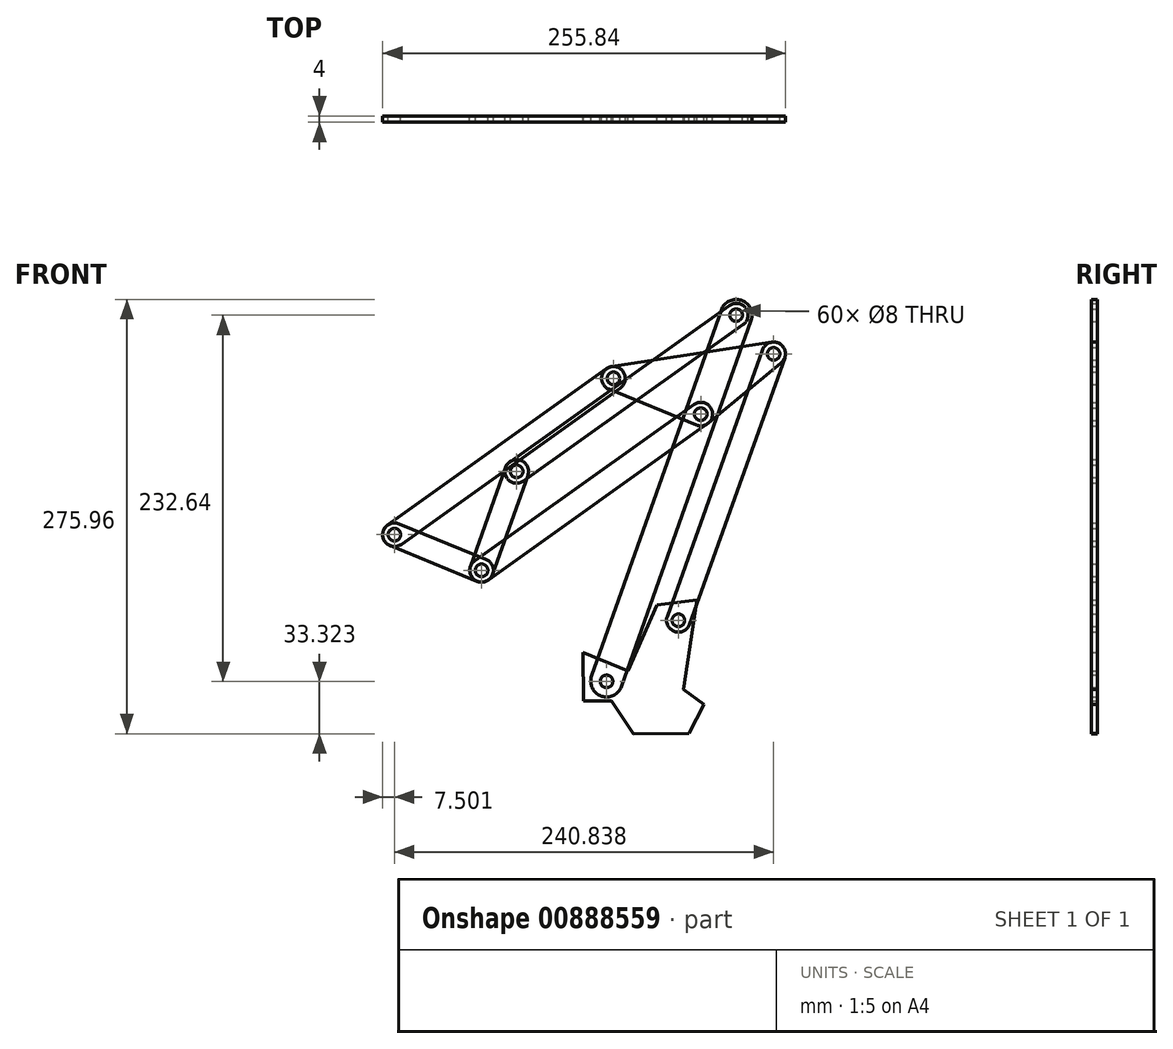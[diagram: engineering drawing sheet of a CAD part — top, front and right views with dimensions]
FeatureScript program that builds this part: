
annotation { "Feature Type Name" : "Feature", "Feature Type Description" : "" }
export const myFeature = defineFeature(function(context is Context, id is Id, definition is map)
    precondition{}
    {
        {
            var Q0;
            Q0=qCreatedBy(makeId("Front.planeOp"),FACE);
            var sketch = newSketch(context, id + "F0", { "sketchPlane" : qUnion([Q0])});
            skCircle(sketch, "E0", {"center": v(-65.08, -32.12) * mm, "radius": 6 * mm});
            skCircle(sketch, "E1", {"center": v(-120.42, -9.5) * mm, "radius": 6 * mm});
            skLineSegment(sketch, "E2", {"start": v(-120.42, -9.5) * mm, "end": v(-65.08, -32.12) * mm});
            skLineSegment(sketch, "E3", {"start": v(-65.08, -32.12) * mm, "end": v(74.1, 67.1) * mm});
            skCircle(sketch, "E4", {"center": v(74.1, 67.1) * mm, "radius": 6 * mm});
            skCircle(sketch, "E5", {"center": v(-42.78, 30.7) * mm, "radius": 6 * mm});
            skLineSegment(sketch, "E6", {"start": v(-65.08, -32.12) * mm, "end": v(-42.78, 30.7) * mm});
            skLineSegment(sketch, "E7", {"start": v(18.68, 89.85) * mm, "end": v(-120.42, -9.5) * mm});
            skCircle(sketch, "E8", {"center": v(18.68, 89.85) * mm, "radius": 6 * mm});
            skLineSegment(sketch, "E9", {"start": v(74.1, 67.1) * mm, "end": v(14.28, -102.66) * mm});
            skLineSegment(sketch, "E10", {"start": v(96.64, 129.98) * mm, "end": v(74.1, 67.1) * mm});
            skCircle(sketch, "E11", {"center": v(120.42, 105.37) * mm, "radius": 6 * mm});
            skLineSegment(sketch, "E12", {"start": v(120.42, 105.37) * mm, "end": v(18.68, 89.85) * mm});
            skLineSegment(sketch, "E13", {"start": v(74.1, 67.1) * mm, "end": v(120.42, 105.37) * mm});
            skLineSegment(sketch, "E14", {"start": v(18.68, 89.85) * mm, "end": v(74.1, 67.1) * mm});
            skLineSegment(sketch, "E15", {"start": v(96.64, 129.98) * mm, "end": v(-42.78, 30.7) * mm});
            skLineSegment(sketch, "E16", {"start": v(120.42, 105.37) * mm, "end": v(59.92, -63.84) * mm});
            skCircle(sketch, "E17", {"center": v(14.28, -102.66) * mm, "radius": 6 * mm});
            skCircle(sketch, "E18", {"center": v(59.92, -63.84) * mm, "radius": 6 * mm});
            skLineSegment(sketch, "E19", {"start": v(-0.52, -84.13) * mm, "end": v(-0.28, -115.17) * mm});
            skLineSegment(sketch, "E20", {"start": v(-0.28, -115.17) * mm, "end": v(17.4, -115.04) * mm});
            skLineSegment(sketch, "E21", {"start": v(17.4, -115.04) * mm, "end": v(31.55, -135.98) * mm});
            skLineSegment(sketch, "E22", {"start": v(31.55, -135.98) * mm, "end": v(66.6, -135.71) * mm});
            skLineSegment(sketch, "E23", {"start": v(66.6, -135.71) * mm, "end": v(76.3, -117.34) * mm});
            skLineSegment(sketch, "E24", {"start": v(76.3, -117.34) * mm, "end": v(63, -107.76) * mm});
            skLineSegment(sketch, "E25", {"start": v(63, -107.76) * mm, "end": v(71.78, -50.98) * mm});
            skLineSegment(sketch, "E26", {"start": v(71.78, -50.98) * mm, "end": v(46.28, -54.1) * mm});
            skLineSegment(sketch, "E27", {"start": v(46.28, -54.1) * mm, "end": v(28.01, -95.9) * mm});
            skLineSegment(sketch, "E28", {"start": v(28.01, -95.9) * mm, "end": v(-0.52, -84.13) * mm});
            skCircle(sketch, "E29", {"center": v(96.64, 129.98) * mm, "radius": 6 * mm});
            skSolve(sketch);
        }
        {
            var Q0;
            Q0=qCreatedBy(makeId("Front.planeOp"),FACE);
            var sketch = newSketch(context, id + "F1", { "sketchPlane" : qUnion([Q0])});
            skCircle(sketch, "E30", {"center": v(-120.42, -9.5) * mm, "radius": 4 * mm});
            skCircle(sketch, "E31", {"center": v(-65.08, -32.12) * mm, "radius": 4 * mm});
            skArc(sketch, "E32", {"start": v(-67.92, -39.07) * mm, "mid": v(-58.14, -34.96) * mm, "end": v(-62.25, -25.18) * mm});
            skArc(sketch, "E33", {"start": v(-117.58, -2.56) * mm, "mid": v(-127.36, -6.66) * mm, "end": v(-123.26, -16.44) * mm});
            skLineSegment(sketch, "E34", {"start": v(-123.26, -16.44) * mm, "end": v(-67.92, -39.07) * mm});
            skLineSegment(sketch, "E35", {"start": v(-117.58, -2.56) * mm, "end": v(-62.25, -25.18) * mm});
            skCircle(sketch, "E36.0", {"center": v(-120.42, -9.5) * mm, "radius": 6 * mm, "construction": true});
            skCircle(sketch, "E37.0", {"center": v(-65.08, -32.12) * mm, "radius": 6 * mm, "construction": true});
            skSolve(sketch);
        }
        {
            var Q0;
            Q0=makeQuery(id+"F1.imprint","IMPRINT",FACE,{"disambiguationData":[TD([[makeQuery(id+"F1.imprint","IMPRINT",EDGE,{"derivedFrom":sQuery(id+"F1.wireOp",EDGE,"E30")}),-1.0]])]});
            extrude(context, id + "F2", {"entities" : qUnion([Q0]), "depth" : 4 * mm, "offsetDistance" : 25 * mm});
        }
        {
            var Q0;
            Q0=qCreatedBy(makeId("Front.planeOp"),FACE);
            var sketch = newSketch(context, id + "F3", { "sketchPlane" : qUnion([Q0])});
            skCircle(sketch, "E38", {"center": v(-42.78, 30.7) * mm, "radius": 4 * mm});
            skArc(sketch, "E39", {"start": v(-72.15, -29.61) * mm, "mid": v(-67.6, -39.2) * mm, "end": v(-58.02, -34.63) * mm});
            skArc(sketch, "E40", {"start": v(-35.7, 28.2) * mm, "mid": v(-40.27, 37.77) * mm, "end": v(-49.84, 33.21) * mm});
            skCircle(sketch, "E41", {"center": v(-65.08, -32.12) * mm, "radius": 4 * mm});
            skLineSegment(sketch, "E42", {"start": v(-35.7, 28.2) * mm, "end": v(-58.02, -34.63) * mm});
            skLineSegment(sketch, "E43", {"start": v(-49.84, 33.21) * mm, "end": v(-72.15, -29.61) * mm});
            skCircle(sketch, "E44.0", {"center": v(-42.78, 30.7) * mm, "radius": 6 * mm, "construction": true});
            skCircle(sketch, "E45.0", {"center": v(-65.08, -32.12) * mm, "radius": 6 * mm, "construction": true});
            skSolve(sketch);
        }
        {
            var Q0;
            Q0=makeQuery(id+"F3.imprint","IMPRINT",FACE,{"disambiguationData":[TD([[makeQuery(id+"F3.imprint","IMPRINT",EDGE,{"derivedFrom":sQuery(id+"F3.wireOp",EDGE,"E38")}),-1.0]])]});
            extrude(context, id + "F4", {"entities" : qUnion([Q0]), "depth" : 4 * mm, "offsetDistance" : 25 * mm});
        }
        {
            var Q0;
            Q0=qCreatedBy(makeId("Front.planeOp"),FACE);
            var sketch = newSketch(context, id + "F5", { "sketchPlane" : qUnion([Q0])});
            skCircle(sketch, "E46", {"center": v(-120.42, -9.5) * mm, "radius": 4 * mm});
            skArc(sketch, "E47", {"start": v(-124.78, -3.4) * mm, "mid": v(-126.52, -13.86) * mm, "end": v(-116.06, -15.6) * mm});
            skArc(sketch, "E48", {"start": v(23.04, 83.75) * mm, "mid": v(24.78, 94.2) * mm, "end": v(14.32, 95.95) * mm});
            skCircle(sketch, "E49", {"center": v(18.68, 89.85) * mm, "radius": 4 * mm});
            skLineSegment(sketch, "E50", {"start": v(-124.78, -3.4) * mm, "end": v(14.32, 95.95) * mm});
            skLineSegment(sketch, "E51", {"start": v(-116.06, -15.6) * mm, "end": v(23.04, 83.75) * mm});
            skCircle(sketch, "E52.0", {"center": v(18.68, 89.85) * mm, "radius": 6 * mm, "construction": true});
            skCircle(sketch, "E53.0", {"center": v(-120.42, -9.5) * mm, "radius": 6 * mm, "construction": true});
            skSolve(sketch);
        }
        {
            var Q0;
            Q0=makeQuery(id+"F5.imprint","IMPRINT",FACE,{"disambiguationData":[TD([[makeQuery(id+"F5.imprint","IMPRINT",EDGE,{"derivedFrom":sQuery(id+"F5.wireOp",EDGE,"E46")}),-1.0]])]});
            extrude(context, id + "F6", {"entities" : qUnion([Q0]), "depth" : 4 * mm, "offsetDistance" : 25 * mm});
        }
        {
            var Q0;
            Q0=qCreatedBy(makeId("Front.planeOp"),FACE);
            var sketch = newSketch(context, id + "F7", { "sketchPlane" : qUnion([Q0])});
            skCircle(sketch, "E54", {"center": v(74.1, 67.1) * mm, "radius": 4 * mm});
            skArc(sketch, "E55", {"start": v(78.46, 60.98) * mm, "mid": v(80.22, 71.44) * mm, "end": v(69.75, 73.2) * mm});
            skCircle(sketch, "E56", {"center": v(-65.08, -32.12) * mm, "radius": 4 * mm});
            skArc(sketch, "E57", {"start": v(-69.44, -26.02) * mm, "mid": v(-71.2, -36.48) * mm, "end": v(-60.73, -38.23) * mm});
            skLineSegment(sketch, "E58", {"start": v(-69.44, -26.02) * mm, "end": v(69.75, 73.2) * mm});
            skLineSegment(sketch, "E59", {"start": v(-60.73, -38.23) * mm, "end": v(78.46, 60.98) * mm});
            skSolve(sketch);
        }
        {
            var Q0;
            Q0=makeQuery(id+"F7.imprint","IMPRINT",FACE,{"disambiguationData":[TD([[makeQuery(id+"F7.imprint","IMPRINT",EDGE,{"derivedFrom":sQuery(id+"F7.wireOp",EDGE,"E54")}),-1.0]])]});
            extrude(context, id + "F8", {"entities" : qUnion([Q0]), "depth" : 4 * mm, "offsetDistance" : 25 * mm});
        }
        {
            var Q0;
            Q0=qCreatedBy(makeId("Front.planeOp"),FACE);
            var sketch = newSketch(context, id + "F9", { "sketchPlane" : qUnion([Q0])});
            skArc(sketch, "E60", {"start": v(71.26, 60.15) * mm, "mid": v(75.23, 59.68) * mm, "end": v(78.89, 61.31) * mm});
            skArc(sketch, "E61", {"start": v(125.2, 99.6) * mm, "mid": v(127.26, 108.44) * mm, "end": v(119.29, 112.79) * mm});
            skArc(sketch, "E62", {"start": v(17.55, 97.26) * mm, "mid": v(11.23, 90.74) * mm, "end": v(15.83, 82.91) * mm});
            skLineSegment(sketch, "E63", {"start": v(15.83, 82.91) * mm, "end": v(71.26, 60.15) * mm});
            skLineSegment(sketch, "E64", {"start": v(17.55, 97.26) * mm, "end": v(119.29, 112.79) * mm});
            skLineSegment(sketch, "E65.trimOffspring", {"start": v(78.89, 61.31) * mm, "end": v(125.2, 99.6) * mm});
            skCircle(sketch, "E66", {"center": v(120.42, 105.37) * mm, "radius": 4 * mm});
            skCircle(sketch, "E67", {"center": v(74.1, 67.1) * mm, "radius": 4 * mm});
            skCircle(sketch, "E68", {"center": v(18.68, 89.85) * mm, "radius": 4 * mm});
            skSolve(sketch);
        }
        {
            var Q0;
            Q0=makeQuery(id+"F9.imprint","IMPRINT",FACE,{"disambiguationData":[TD([[makeQuery(id+"F9.imprint","IMPRINT",EDGE,{"derivedFrom":sQuery(id+"F9.wireOp",EDGE,"E60")}),1.0]])]});
            extrude(context, id + "F10", {"entities" : qUnion([Q0]), "depth" : 4 * mm, "offsetDistance" : 25 * mm});
        }
        {
            var Q0;
            Q0=qCreatedBy(makeId("Front.planeOp"),FACE);
            var sketch = newSketch(context, id + "F11", { "sketchPlane" : qUnion([Q0])});
            skCircle(sketch, "E69.0", {"center": v(96.64, 129.98) * mm, "radius": 6 * mm, "construction": true});
            skCircle(sketch, "E70.0", {"center": v(74.1, 67.1) * mm, "radius": 6 * mm, "construction": true});
            skCircle(sketch, "E71.0", {"center": v(14.28, -102.66) * mm, "radius": 6 * mm, "construction": true});
            skCircle(sketch, "E72", {"center": v(14.28, -102.66) * mm, "radius": 4 * mm});
            skCircle(sketch, "E73", {"center": v(74.1, 67.1) * mm, "radius": 4 * mm});
            skCircle(sketch, "E74", {"center": v(96.64, 129.98) * mm, "radius": 4 * mm});
            skArc(sketch, "E75", {"start": v(106.07, 126.65) * mm, "mid": v(99.98, 139.41) * mm, "end": v(87.21, 133.32) * mm});
            skArc(sketch, "E76", {"start": v(4.86, -99.32) * mm, "mid": v(10.95, -112.08) * mm, "end": v(23.7, -106) * mm});
            skLineSegment(sketch, "E77", {"start": v(106.07, 126.65) * mm, "end": v(23.7, -106) * mm});
            skLineSegment(sketch, "E78", {"start": v(87.21, 133.32) * mm, "end": v(4.86, -99.32) * mm});
            skSolve(sketch);
        }
        {
            var Q0;
            Q0 = qSketchRegion(id + "F11", true);
            extrude(context, id + "F12", {"entities" : qUnion([Q0]), "depth" : 4 * mm, "offsetDistance" : 25 * mm});
        }
        {
            var Q0;
            Q0=qCreatedBy(makeId("Front.planeOp"),FACE);
            var sketch = newSketch(context, id + "F13", { "sketchPlane" : qUnion([Q0])});
            skCircle(sketch, "E79.0", {"center": v(-42.78, 30.7) * mm, "radius": 6 * mm, "construction": true});
            skCircle(sketch, "E80.0", {"center": v(96.64, 129.98) * mm, "radius": 6 * mm, "construction": true});
            skArc(sketch, "E81", {"start": v(-47.13, 36.81) * mm, "mid": v(-48.88, 26.35) * mm, "end": v(-38.43, 24.6) * mm});
            skArc(sketch, "E82", {"start": v(101, 123.87) * mm, "mid": v(102.75, 134.33) * mm, "end": v(92.3, 136.1) * mm});
            skCircle(sketch, "E83", {"center": v(96.64, 129.98) * mm, "radius": 4 * mm});
            skCircle(sketch, "E84", {"center": v(-42.78, 30.7) * mm, "radius": 4 * mm});
            skLineSegment(sketch, "E85", {"start": v(-47.13, 36.81) * mm, "end": v(92.3, 136.1) * mm});
            skLineSegment(sketch, "E86", {"start": v(101, 123.87) * mm, "end": v(-38.43, 24.6) * mm});
            skSolve(sketch);
        }
        {
            var Q0;
            Q0=makeQuery(id+"F13.imprint","IMPRINT",FACE,{"disambiguationData":[TD([[makeQuery(id+"F13.imprint","IMPRINT",EDGE,{"derivedFrom":sQuery(id+"F13.wireOp",EDGE,"E81")}),1.0]])]});
            extrude(context, id + "F14", {"entities" : qUnion([Q0]), "depth" : 4 * mm, "offsetDistance" : 25 * mm});
        }
        {
            var Q0;
            Q0=qCreatedBy(makeId("Front.planeOp"),FACE);
            var sketch = newSketch(context, id + "F15", { "sketchPlane" : qUnion([Q0])});
            skCircle(sketch, "E87", {"center": v(120.42, 105.37) * mm, "radius": 4 * mm});
            skArc(sketch, "E88", {"start": v(127.48, 102.85) * mm, "mid": v(122.94, 112.44) * mm, "end": v(113.36, 107.9) * mm});
            skCircle(sketch, "E89", {"center": v(59.92, -63.84) * mm, "radius": 4 * mm});
            skArc(sketch, "E90", {"start": v(52.86, -61.32) * mm, "mid": v(57.4, -70.9) * mm, "end": v(66.99, -66.37) * mm});
            skLineSegment(sketch, "E91", {"start": v(52.86, -61.32) * mm, "end": v(113.36, 107.9) * mm});
            skLineSegment(sketch, "E92", {"start": v(127.48, 102.85) * mm, "end": v(66.99, -66.37) * mm});
            skSolve(sketch);
        }
        {
            var Q0;
            Q0=makeQuery(id+"F15.imprint","IMPRINT",FACE,{"disambiguationData":[TD([[makeQuery(id+"F15.imprint","IMPRINT",EDGE,{"derivedFrom":sQuery(id+"F15.wireOp",EDGE,"E87")}),-1.0]])]});
            extrude(context, id + "F16", {"entities" : qUnion([Q0]), "depth" : 4 * mm, "offsetDistance" : 25 * mm});
        }
        {
            var Q0;
            Q0=qCreatedBy(makeId("Front.planeOp"),FACE);
            var sketch = newSketch(context, id + "F17", { "sketchPlane" : qUnion([Q0])});
            skLineSegment(sketch, "E93.0", {"start": v(46.28, -54.1) * mm, "end": v(28.01, -95.9) * mm, "construction": true});
            skLineSegment(sketch, "E94.0", {"start": v(71.78, -50.98) * mm, "end": v(46.28, -54.1) * mm, "construction": true});
            skLineSegment(sketch, "E95.0", {"start": v(63, -107.76) * mm, "end": v(71.78, -50.98) * mm, "construction": true});
            skLineSegment(sketch, "E96.0", {"start": v(76.3, -117.34) * mm, "end": v(63, -107.76) * mm, "construction": true});
            skLineSegment(sketch, "E97.0", {"start": v(66.6, -135.71) * mm, "end": v(76.3, -117.34) * mm, "construction": true});
            skLineSegment(sketch, "E98.0", {"start": v(31.55, -135.98) * mm, "end": v(66.6, -135.71) * mm, "construction": true});
            skLineSegment(sketch, "E99.0", {"start": v(17.4, -115.04) * mm, "end": v(31.55, -135.98) * mm, "construction": true});
            skLineSegment(sketch, "E100.0", {"start": v(-0.28, -115.17) * mm, "end": v(17.4, -115.04) * mm, "construction": true});
            skLineSegment(sketch, "E101.0", {"start": v(-0.52, -84.13) * mm, "end": v(-0.28, -115.17) * mm, "construction": true});
            skLineSegment(sketch, "E102.0", {"start": v(28.01, -95.9) * mm, "end": v(-0.52, -84.13) * mm, "construction": true});
            skCircle(sketch, "E103.0", {"center": v(59.92, -63.84) * mm, "radius": 6 * mm, "construction": true});
            skCircle(sketch, "E104.0", {"center": v(14.28, -102.66) * mm, "radius": 6 * mm, "construction": true});
            skLineSegment(sketch, "E105", {"start": v(-0.52, -84.13) * mm, "end": v(28.01, -95.9) * mm});
            skLineSegment(sketch, "E106", {"start": v(46.28, -54.1) * mm, "end": v(28.01, -95.9) * mm});
            skLineSegment(sketch, "E107", {"start": v(46.28, -54.1) * mm, "end": v(71.78, -50.98) * mm});
            skLineSegment(sketch, "E108", {"start": v(63, -107.76) * mm, "end": v(76.3, -117.34) * mm});
            skLineSegment(sketch, "E109", {"start": v(71.78, -50.98) * mm, "end": v(63, -107.76) * mm});
            skLineSegment(sketch, "E110", {"start": v(-0.52, -84.13) * mm, "end": v(-0.28, -115.17) * mm});
            skLineSegment(sketch, "E111", {"start": v(-0.28, -115.17) * mm, "end": v(17.4, -115.04) * mm});
            skLineSegment(sketch, "E112", {"start": v(17.4, -115.04) * mm, "end": v(31.55, -135.98) * mm});
            skLineSegment(sketch, "E113", {"start": v(31.55, -135.98) * mm, "end": v(66.6, -135.71) * mm});
            skLineSegment(sketch, "E114", {"start": v(66.6, -135.71) * mm, "end": v(76.3, -117.34) * mm});
            skCircle(sketch, "E115", {"center": v(14.28, -102.66) * mm, "radius": 4 * mm});
            skCircle(sketch, "E116", {"center": v(59.92, -63.84) * mm, "radius": 4 * mm});
            skSolve(sketch);
        }
        {
            var Q0;
            Q0=makeQuery(id+"F17.imprint","IMPRINT",FACE,{"disambiguationData":[TD([[makeQuery(id+"F17.imprint","IMPRINT",EDGE,{"derivedFrom":sQuery(id+"F17.wireOp",EDGE,"E105")}),-1.0]])]});
            extrude(context, id + "F18", {"entities" : qUnion([Q0]), "depth" : 4 * mm, "offsetDistance" : 25 * mm});
        }
    });
